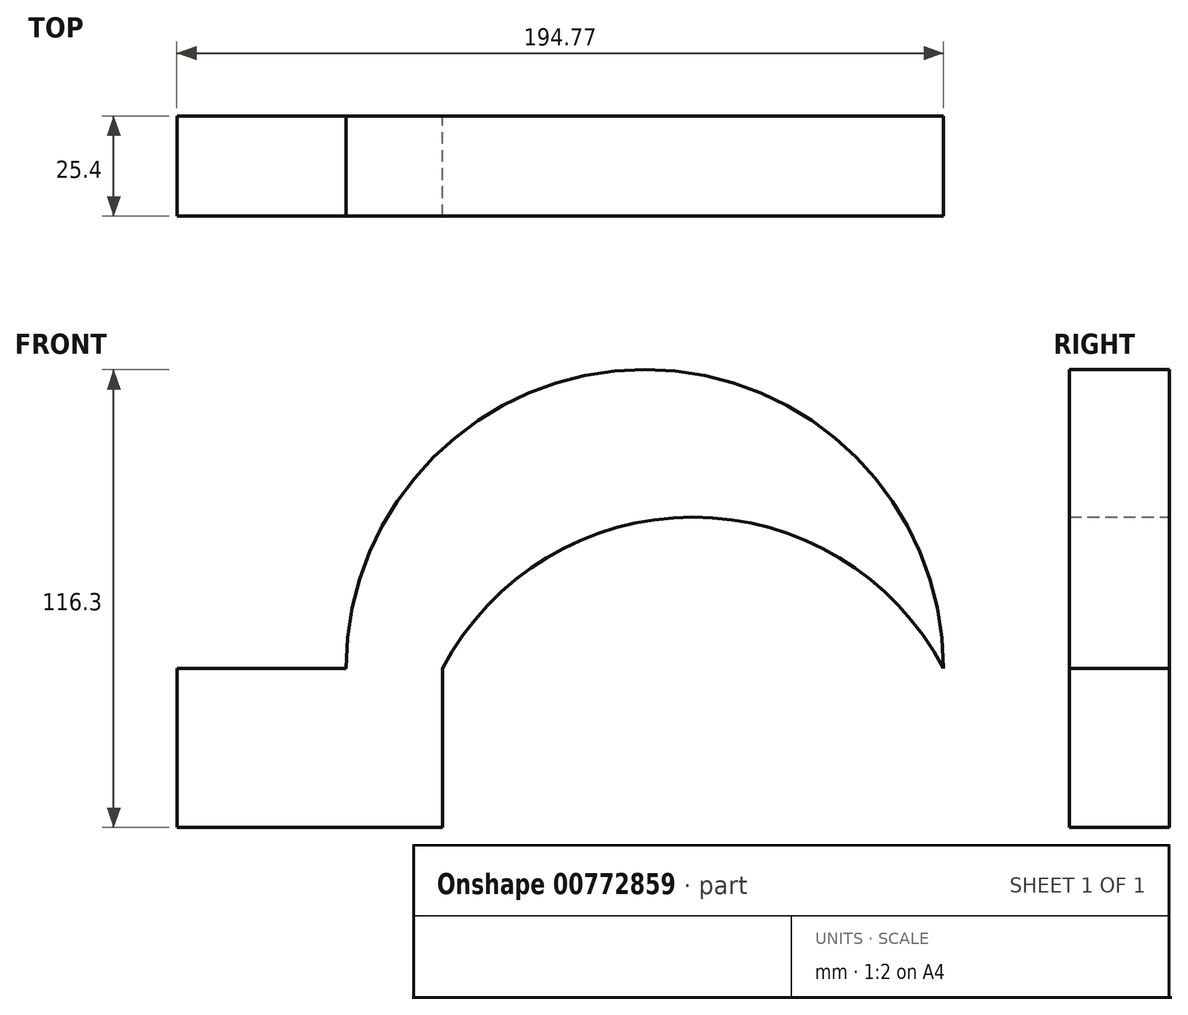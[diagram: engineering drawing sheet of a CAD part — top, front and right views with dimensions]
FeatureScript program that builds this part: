
annotation { "Feature Type Name" : "Feature", "Feature Type Description" : "" }
export const myFeature = defineFeature(function(context is Context, id is Id, definition is map)
    precondition{}
    {
        {
            var Q0;
            Q0=qCreatedBy(makeId("Front.planeOp"),FACE);
            var sketch = newSketch(context, id + "F0", { "sketchPlane" : qUnion([Q0])});
            skPoint(sketch, "E0.start.orphan", {"position": v(-54.28, 38.46) * mm});
            skPoint(sketch, "E1.end.orphan", {"position": v(-54.28, 48.56) * mm});
            skLineSegment(sketch, "E2.bottom", {"start": v(-56.48, 27.03) * mm, "end": v(-13.45, 27.03) * mm});
            skLineSegment(sketch, "E2.top", {"start": v(-56.48, -13.4) * mm, "end": v(11.03, -13.4) * mm});
            skLineSegment(sketch, "E2.left", {"start": v(-56.48, 27.03) * mm, "end": v(-56.48, -13.4) * mm});
            skLineSegment(sketch, "E2.right", {"start": v(11.03, 27.03) * mm, "end": v(11.03, -13.4) * mm});
            skArc(sketch, "E3", {"start": v(138.3, 27.03) * mm, "mid": v(74.66, 65.44) * mm, "end": v(11.03, 27.03) * mm});
            skArc(sketch, "E4", {"start": v(138.3, 27.03) * mm, "mid": v(62.42, 102.9) * mm, "end": v(-13.45, 27.03) * mm});
            skSolve(sketch);
        }
        {
            var Q0;
            Q0 = qSketchRegion(id + "F0", true);
            extrude(context, id + "F1", {"entities" : qUnion([Q0]), "depth" : 25.4 * mm, "offsetDistance" : 25.4 * mm});
        }
    });
